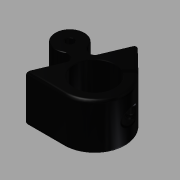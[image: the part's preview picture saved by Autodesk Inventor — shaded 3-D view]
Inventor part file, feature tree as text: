
AUTODESK INVENTOR PART (.ipt)
format: ipt  version: 2014 (Build 180170000, 170)  size: 612,352 bytes
history: native  units: mm
features: sketch x7, extrude x6, fillet x6, projected_geometry x5, delete_face x4, plane x1, mirror x1, split x1
ambient origin geometry x8: Origin, YZ Plane, XZ Plane, XY Plane, X Axis, Y Axis, Z Axis, Center Point
bodies: Body1 (feature_tree), Body2 (feature_tree), Body3 (feature_tree)
feature tree (31):
  extrude  "Extrusion2"  Depth=226.0mm
  extrude  "Extrusion5"  Depth=26.0mm
  fillet  "Fillet1"  Radius=26.0mm
  sketch  "Sketch4"  dims[d14=20.0mm d17=20.0mm]
  extrude  "Extrusion7"  Depth=20.0mm
  extrude  "Extrusion8"  Depth=20.0mm
  extrude  "Extrusion9"  Depth=20.0mm
  plane  "Work Plane3"
  extrude  "Extrusion10"  Depth=5.0mm
  fillet  "Fillet4"  Radius=22.0mm
  fillet  "Fillet5"  Radius=30.0mm
  mirror  "Mirror1"
  fillet  "Fillet6"  Radius=30.0mm
  fillet  "Fillet7"  Radius=19.0mm
  split  "Split1"
  delete_face  "Delete Face1"
  delete_face  "Delete Face2"
  delete_face  "Delete Face3"
  delete_face  "Delete Face4"
  fillet  "Fillet8"  Radius=5.0mm
  sketch  "Sketch1"  dims[d0=113.0mm d1=226.0mm]
  sketch  "Sketch2"  dims[d2=110.0mm d3=26.0mm d5=26.0mm]
  projected_geometry  "Projected Loop1"
  projected_geometry  "Projected Loop3"
  sketch  "Sketch5"  dims[d18=20.0mm d19=25.0mm]
  projected_geometry  "Projected Loop4"
  sketch  "Sketch6"  dims[d20=20.0mm d21=25.0mm]
  projected_geometry  "Projected Loop5"
  sketch  "Sketch7"  dims[d22=25.0mm d23=25.0mm d24=22.0mm d27=30.0mm d28=0.0mm d33=30.0mm d34=19.0mm d35=5.0mm]
  projected_geometry  "Projected Loop6"
  sketch  "Sketch9"  dims[d41=5.0mm d42=5.0mm d43=20.0mm d44=0.0mm d45=3.0mm d46=35.0mm d47=20.0mm d48=7.0mm d49=14.0mm d50=7.0mm d51=14.0mm d52=1.0mm d53=1.0mm d54=5.0mm d58=2.8mm d59=9.0mm d60=20.0mm d61=0.0mm d62=4.0mm d63=4.1mm d64=30.0mm d65=0.0mm d66=7.5mm d67=2.5mm d68=15.0mm d69=0.0mm d71=5.0mm d72=0.0mm d74=-9.5mm d75=7.5mm d76=15.0mm d77=0.0mm d79=2.0mm d80=0.5mm d81=2.0mm d82=2.0mm d83=0.5mm]
